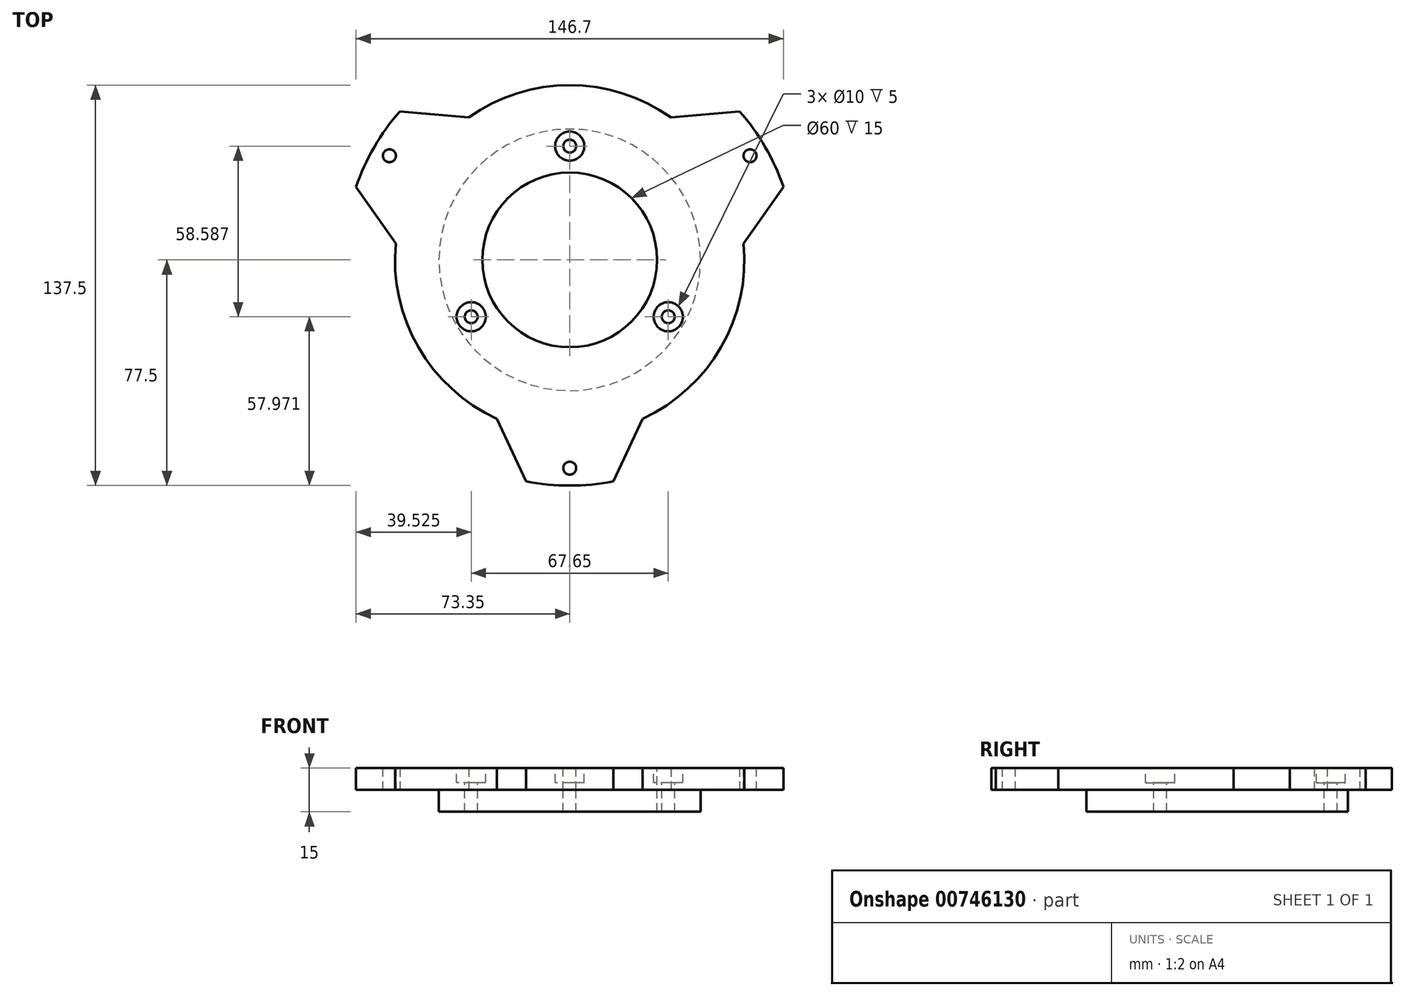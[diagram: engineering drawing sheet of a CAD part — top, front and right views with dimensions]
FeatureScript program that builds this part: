
annotation { "Feature Type Name" : "Feature", "Feature Type Description" : "" }
export const myFeature = defineFeature(function(context is Context, id is Id, definition is map)
    precondition{}
    {
        {
            var Q0;
            Q0=qCreatedBy(makeId("Top.planeOp"),FACE);
            var sketch = newSketch(context, id + "F0", { "sketchPlane" : qUnion([Q0])});
            skCircle(sketch, "E0", {"center": v(0, 0) * mm, "radius": 44.9 * mm});
            skCircle(sketch, "E1", {"center": v(0, 0) * mm, "radius": 25 * mm});
            skSolve(sketch);
        }
        {
            var Q0;
            Q0=qCreatedBy(makeId("Top.planeOp"),FACE);
            var sketch = newSketch(context, id + "F1", { "sketchPlane" : qUnion([Q0])});
            skCircle(sketch, "E2", {"center": v(0, 0) * mm, "radius": 77.5 * mm});
            skCircle(sketch, "E3", {"center": v(0, 0) * mm, "radius": 72.5 * mm, "construction": true});
            skCircle(sketch, "E4", {"center": v(0, 0) * mm, "radius": 60 * mm});
            skLineSegment(sketch, "E5", {"start": v(0, 0) * mm, "end": v(0, -98.48) * mm, "construction": true});
            skLineSegment(sketch, "E6", {"start": v(-25, -54.54) * mm, "end": v(-15, -76.03) * mm});
            skLineSegment(sketch, "E7.MirrorCS", {"start": v(25, -54.54) * mm, "end": v(15, -76.03) * mm});
            skLineSegment(sketch, "E8.1.0", {"start": v(59.74, 5.62) * mm, "end": v(73.35, 25.03) * mm});
            skLineSegment(sketch, "E8.1.1", {"start": v(34.74, 48.92) * mm, "end": v(58.35, 51) * mm});
            skLineSegment(sketch, "E8.2.0", {"start": v(-34.74, 48.92) * mm, "end": v(-58.35, 51) * mm});
            skLineSegment(sketch, "E8.2.1", {"start": v(-59.74, 5.62) * mm, "end": v(-73.35, 25.03) * mm});
            skSolve(sketch);
        }
        {
            var Q0;
            {var subQ0=sQuery(id+"F1.wireOp",EDGE,"E4");var subQ5=makeQuery(id+"F1.imprint","INTERSECT",VERTEX,{"derivedFrom":[subQ0,sQuery(id+"F1.wireOp",EDGE,"E8.1.0")]});Q0=makeQuery(id+"F1.imprint","IMPRINT",FACE,{"disambiguationData":[TD([[makeQuery(id+"F1.imprint","IMPRINT",EDGE,{"disambiguationData":[TD([[subQ5,-1.0]])],"derivedFrom":subQ0}),1.0]])]});}
            var Q1;
            {var subQ0=sQuery(id+"F1.wireOp",EDGE,"E8.2.0");Q1=makeQuery(id+"F1.imprint","IMPRINT",FACE,{"disambiguationData":[TD([[makeQuery(id+"F1.imprint","IMPRINT",EDGE,{"derivedFrom":subQ0}),1.0]])]});}
            var Q2;
            {var subQ0=sQuery(id+"F1.wireOp",EDGE,"E6");Q2=makeQuery(id+"F1.imprint","IMPRINT",FACE,{"disambiguationData":[TD([[makeQuery(id+"F1.imprint","IMPRINT",EDGE,{"derivedFrom":subQ0}),1.0]])]});}
            var Q3;
            {var subQ0=sQuery(id+"F1.wireOp",EDGE,"E8.1.0");Q3=makeQuery(id+"F1.imprint","IMPRINT",FACE,{"disambiguationData":[TD([[makeQuery(id+"F1.imprint","IMPRINT",EDGE,{"derivedFrom":subQ0}),1.0]])]});}
            extrude(context, id + "F2", {"entities" : qUnion([Q0, Q1, Q2, Q3]), "depth" : 7.5 * mm, "offsetDistance" : 25 * mm});
        }
        {
            var Q0;
            Q0=qSketchRegion(id+"F0",true);
            var Q1;
            Q1=makeQuery(id+"F0.imprint","IMPRINT",FACE,{"disambiguationData":[TD([[makeQuery(id+"F0.imprint","IMPRINT",EDGE,{"derivedFrom":sQuery(id+"F0.wireOp",EDGE,"E1")}),1.0]])]});
            extrude(context, id + "F3", {"entities" : qUnion([Q0, Q1]), "operationType" : NewBodyOperationType.ADD, "oppositeDirection" : true, "depth" : 7.5 * mm, "offsetDistance" : 25 * mm});
        }
        {
            var Q0;
            Q0=makeQuery(id+"F2.opExtrude","CAP_FACE",FACE,{"disambiguationData":[OSD([sQuery(id+"F1.wireOp",EDGE,"E2"),sQuery(id+"F1.wireOp",EDGE,"E4"),sQuery(id+"F1.wireOp",EDGE,"E6"),sQuery(id+"F1.wireOp",EDGE,"E7.MirrorCS"),sQuery(id+"F1.wireOp",EDGE,"E8.1.0"),sQuery(id+"F1.wireOp",EDGE,"E8.1.1"),sQuery(id+"F1.wireOp",EDGE,"E8.2.0"),sQuery(id+"F1.wireOp",EDGE,"E8.2.1")])],"isStart":false});
            var sketch = newSketch(context, id + "F4", { "sketchPlane" : qUnion([Q0])});
            skCircle(sketch, "E9", {"center": v(0, 0) * mm, "radius": 44.9 * mm});
            skCircle(sketch, "E10", {"center": v(0, 0) * mm, "radius": 36 * mm});
            skPoint(sketch, "E11", {"position": v(0, 39.06) * mm});
            skCircle(sketch, "E12", {"center": v(0, 39.06) * mm, "radius": 2.22 * mm});
            skLineSegment(sketch, "E13", {"start": v(0, 0) * mm, "end": v(0, 54.54) * mm, "construction": true});
            skCircle(sketch, "E14", {"center": v(0, 39.06) * mm, "radius": 5 * mm});
            skCircle(sketch, "E15.1.0", {"center": v(-33.83, -19.53) * mm, "radius": 2.22 * mm});
            skCircle(sketch, "E15.1.1", {"center": v(-33.83, -19.53) * mm, "radius": 5 * mm});
            skCircle(sketch, "E15.2.0", {"center": v(33.83, -19.53) * mm, "radius": 2.22 * mm});
            skCircle(sketch, "E15.2.1", {"center": v(33.83, -19.53) * mm, "radius": 5 * mm});
            skSolve(sketch);
        }
        {
            var Q0;
            Q0=makeQuery(id+"F4.imprint","IMPRINT",FACE,{"disambiguationData":[TD([[makeQuery(id+"F4.imprint","IMPRINT",EDGE,{"derivedFrom":sQuery(id+"F4.wireOp",EDGE,"E15.1.0")}),1.0]])]});
            var Q1;
            Q1=makeQuery(id+"F4.imprint","IMPRINT",FACE,{"disambiguationData":[TD([[makeQuery(id+"F4.imprint","IMPRINT",EDGE,{"derivedFrom":sQuery(id+"F4.wireOp",EDGE,"E12")}),1.0]])]});
            var Q2;
            Q2=makeQuery(id+"F4.imprint","IMPRINT",FACE,{"disambiguationData":[TD([[makeQuery(id+"F4.imprint","IMPRINT",EDGE,{"derivedFrom":sQuery(id+"F4.wireOp",EDGE,"E15.2.0")}),1.0]])]});
            extrude(context, id + "F5", {"entities" : qUnion([Q0, Q1, Q2]), "operationType" : NewBodyOperationType.REMOVE, "oppositeDirection" : true, "depth" : 25 * mm, "offsetDistance" : 25 * mm});
        }
        {
            var Q0;
            Q0=makeQuery(id+"F4.imprint","IMPRINT",FACE,{"disambiguationData":[TD([[makeQuery(id+"F4.imprint","IMPRINT",EDGE,{"derivedFrom":sQuery(id+"F4.wireOp",EDGE,"E15.1.0")}),-1.0]])]});
            var Q1;
            Q1=makeQuery(id+"F4.imprint","IMPRINT",FACE,{"disambiguationData":[TD([[makeQuery(id+"F4.imprint","IMPRINT",EDGE,{"derivedFrom":sQuery(id+"F4.wireOp",EDGE,"E12")}),-1.0]])]});
            var Q2;
            Q2=makeQuery(id+"F4.imprint","IMPRINT",FACE,{"disambiguationData":[TD([[makeQuery(id+"F4.imprint","IMPRINT",EDGE,{"derivedFrom":sQuery(id+"F4.wireOp",EDGE,"E15.2.0")}),-1.0]])]});
            var Q3;
            {var subQ0=sQuery(id+"F4.wireOp",EDGE,"E14");var subQ1=sQuery(id+"F4.wireOp",EDGE,"E10");var subQ2=makeQuery(id+"F4.imprint","INTERSECT",VERTEX,{"disambiguationData":[OD(0.0)],"derivedFrom":[subQ1,subQ0]});Q3=makeQuery(id+"F4.imprint","IMPRINT",FACE,{"disambiguationData":[TD([[makeQuery(id+"F4.imprint","IMPRINT",EDGE,{"disambiguationData":[TD([[subQ2,1.0]])],"derivedFrom":subQ1}),1.0]])]});}
            var Q4;
            {var subQ0=sQuery(id+"F4.wireOp",EDGE,"E15.2.1");var subQ1=sQuery(id+"F4.wireOp",EDGE,"E10");var subQ2=makeQuery(id+"F4.imprint","INTERSECT",VERTEX,{"disambiguationData":[OD(0.0)],"derivedFrom":[subQ1,subQ0]});Q4=makeQuery(id+"F4.imprint","IMPRINT",FACE,{"disambiguationData":[TD([[makeQuery(id+"F4.imprint","IMPRINT",EDGE,{"disambiguationData":[TD([[subQ2,-1.0]])],"derivedFrom":subQ1}),1.0]])]});}
            var Q5;
            {var subQ0=sQuery(id+"F4.wireOp",EDGE,"E15.1.1");var subQ1=sQuery(id+"F4.wireOp",EDGE,"E10");var subQ2=makeQuery(id+"F4.imprint","INTERSECT",VERTEX,{"disambiguationData":[OD(0.0)],"derivedFrom":[subQ1,subQ0]});Q5=makeQuery(id+"F4.imprint","IMPRINT",FACE,{"disambiguationData":[TD([[makeQuery(id+"F4.imprint","IMPRINT",EDGE,{"disambiguationData":[TD([[subQ2,-1.0]])],"derivedFrom":subQ1}),1.0]])]});}
            extrude(context, id + "F6", {"entities" : qUnion([Q0, Q1, Q2, Q3, Q4, Q5]), "operationType" : NewBodyOperationType.REMOVE, "oppositeDirection" : true, "depth" : 5 * mm, "offsetDistance" : 25 * mm});
        }
        {
            var Q0;
            Q0=makeQuery(id+"F3.opExtrude","CAP_FACE",FACE,{"disambiguationData":[OSD([sQuery(id+"F0.wireOp",EDGE,"E0")])],"isStart":false});
            var sketch = newSketch(context, id + "F7", { "sketchPlane" : qUnion([Q0])});
            skCircle(sketch, "E16", {"center": v(0, 0) * mm, "radius": 25 * mm});
            skSolve(sketch);
        }
        {
            var Q0;
            Q0=qSketchRegion(id+"F7",true);
            extrude(context, id + "F8", {"entities" : qUnion([Q0]), "operationType" : NewBodyOperationType.REMOVE, "oppositeDirection" : true, "depth" : 25 * mm, "offsetDistance" : 25 * mm});
        }
        {
            var Q0;
            Q0=makeQuery(id+"F4.imprint","IMPRINT",FACE,{"disambiguationData":[TD([[makeQuery(id+"F4.imprint","IMPRINT",EDGE,{"derivedFrom":sQuery(id+"F4.wireOp",EDGE,"E9")}),-1.0]])]});
            var sketch = newSketch(context, id + "F9", { "sketchPlane" : qUnion([Q0])});
            skCircle(sketch, "E17", {"center": v(0, 0) * mm, "radius": 71.5 * mm, "construction": true});
            skCircle(sketch, "E18", {"center": v(0, 0) * mm, "radius": 30 * mm});
            skLineSegment(sketch, "E19", {"start": v(0, 0) * mm, "end": v(0, -71.5) * mm, "construction": true});
            skPoint(sketch, "E19.endSnap0", {"position": v(0, -77.5) * mm});
            skCircle(sketch, "E20", {"center": v(0, -71.5) * mm, "radius": 2.22 * mm});
            skCircle(sketch, "E21.1.0", {"center": v(61.92, 35.75) * mm, "radius": 2.22 * mm});
            skCircle(sketch, "E21.2.0", {"center": v(-61.92, 35.75) * mm, "radius": 2.22 * mm});
            skSolve(sketch);
        }
        {
            var Q0;
            Q0=qSketchRegion(id+"F9",true);
            extrude(context, id + "F10", {"entities" : qUnion([Q0]), "operationType" : NewBodyOperationType.REMOVE, "oppositeDirection" : true, "depth" : 25 * mm, "offsetDistance" : 25 * mm});
        }
    });
